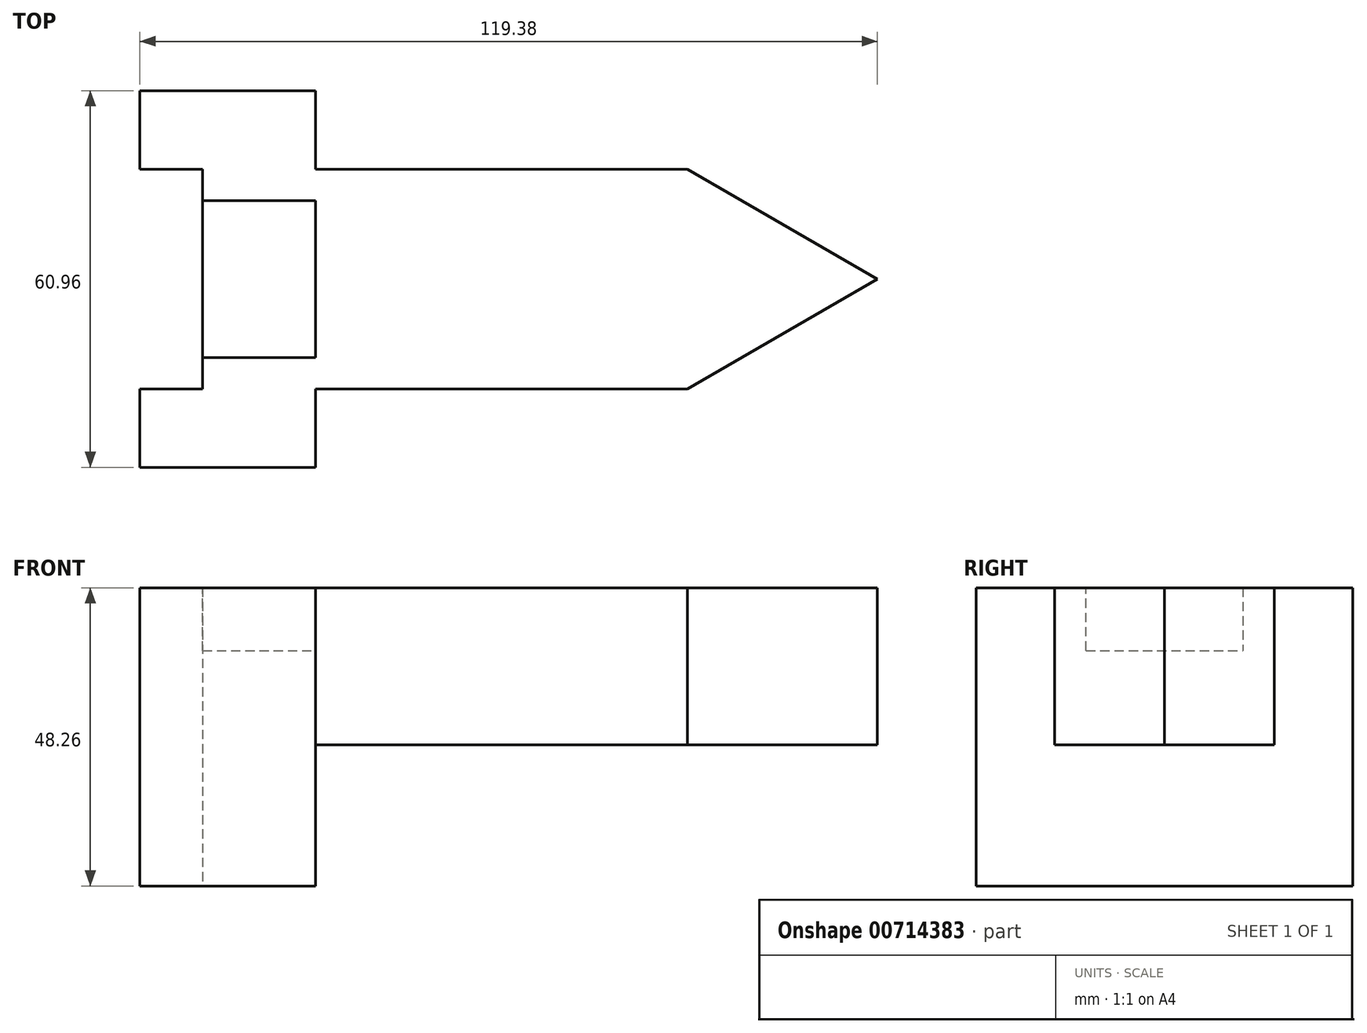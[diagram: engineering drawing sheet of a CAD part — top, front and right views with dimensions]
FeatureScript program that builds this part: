
annotation { "Feature Type Name" : "Feature", "Feature Type Description" : "" }
export const myFeature = defineFeature(function(context is Context, id is Id, definition is map)
    precondition{}
    {
        {
            var Q0;
            Q0=qCreatedBy(makeId("Top.planeOp"),FACE);
            var sketch = newSketch(context, id + "F0", { "sketchPlane" : qUnion([Q0])});
            skLineSegment(sketch, "E0", {"start": v(0, 0) * mm, "end": v(-28.45, 0) * mm});
            skLineSegment(sketch, "E1", {"start": v(-28.45, 0) * mm, "end": v(-28.45, 12.7) * mm});
            skLineSegment(sketch, "E2", {"start": v(-28.45, 12.7) * mm, "end": v(-18.29, 12.7) * mm});
            skLineSegment(sketch, "E3", {"start": v(-18.29, 12.7) * mm, "end": v(-18.29, 17.78) * mm});
            skLineSegment(sketch, "E4", {"start": v(0, 0) * mm, "end": v(0, 30.48) * mm});
            skLineSegment(sketch, "E5", {"start": v(-18.29, 30.48) * mm, "end": v(-18.29, 17.78) * mm});
            skLineSegment(sketch, "E6.MirrorCS", {"start": v(-18.29, 30.48) * mm, "end": v(-18.29, 43.18) * mm});
            skLineSegment(sketch, "E7.MirrorCS", {"start": v(-18.29, 48.26) * mm, "end": v(-18.29, 43.18) * mm});
            skLineSegment(sketch, "E8.MirrorCS", {"start": v(-28.45, 48.26) * mm, "end": v(-18.29, 48.26) * mm});
            skLineSegment(sketch, "E9.MirrorCS", {"start": v(-28.45, 60.96) * mm, "end": v(-28.45, 48.26) * mm});
            skLineSegment(sketch, "E10.MirrorCS", {"start": v(0, 60.96) * mm, "end": v(-28.45, 60.96) * mm});
            skLineSegment(sketch, "E11.MirrorCS", {"start": v(0, 60.96) * mm, "end": v(0, 30.48) * mm});
            skSolve(sketch);
        }
        {
            var Q0;
            Q0 = qSketchRegion(id + "F0", true);
            extrude(context, id + "F1", {"entities" : qUnion([Q0]), "depth" : 48.26 * mm, "offsetDistance" : 25.4 * mm});
        }
        {
            var Q0;
            Q0=makeQuery(id+"F1.opExtrude","SWEPT_FACE",FACE,{"disambiguationData":[OSD([sQuery(id+"F0.wireOp",EDGE,"E4"),sQuery(id+"F0.wireOp",EDGE,"E11.MirrorCS")])]});
            var sketch = newSketch(context, id + "F2", { "sketchPlane" : qUnion([Q0])});
            skLineSegment(sketch, "E12", {"start": v(30.48, 38.1) * mm, "end": v(43.18, 38.1) * mm});
            skLineSegment(sketch, "E13", {"start": v(30.48, 38.1) * mm, "end": v(17.78, 38.1) * mm});
            skLineSegment(sketch, "E14", {"start": v(17.78, 48.26) * mm, "end": v(17.78, 38.1) * mm});
            skLineSegment(sketch, "E15", {"start": v(43.18, 38.1) * mm, "end": v(43.18, 48.26) * mm});
            skLineSegment(sketch, "E16", {"start": v(17.78, 48.26) * mm, "end": v(43.18, 48.26) * mm});
            skSolve(sketch);
        }
        {
            var Q0;
            Q0 = qSketchRegion(id + "F2", true);
            extrude(context, id + "F3", {"entities" : qUnion([Q0]), "operationType" : NewBodyOperationType.REMOVE, "endBound" : BoundingType.UP_TO_NEXT, "oppositeDirection" : true, "depth" : 25.4 * mm, "offsetDistance" : 25.4 * mm});
        }
        {
            var Q0;
            {var subQ0=sQuery(id+"F0.wireOp",EDGE,"E9.MirrorCS");var subQ1=sQuery(id+"F0.wireOp",EDGE,"E8.MirrorCS");var subQ2=sQuery(id+"F0.wireOp",EDGE,"E11.MirrorCS");var subQ3=sQuery(id+"F0.wireOp",EDGE,"E4");var subQ4=sQuery(id+"F0.wireOp",EDGE,"E7.MirrorCS");var subQ5=sQuery(id+"F0.wireOp",EDGE,"E6.MirrorCS");var subQ6=sQuery(id+"F0.wireOp",EDGE,"E5");var subQ7=sQuery(id+"F0.wireOp",EDGE,"E3");var subQ8=sQuery(id+"F0.wireOp",EDGE,"E10.MirrorCS");Q0=makeQuery(id+"F3.boolean.opBoolean","SPLIT",FACE,{"disambiguationData":[TD([makeQuery(id+"F1.opExtrude","SWEPT_FACE",FACE,{"disambiguationData":[OSD([subQ1])]})])],"derivedFrom":makeQuery(id+"F1.opExtrude","CAP_FACE",FACE,{"disambiguationData":[OSD([sQuery(id+"F0.wireOp",EDGE,"E0"),sQuery(id+"F0.wireOp",EDGE,"E1"),sQuery(id+"F0.wireOp",EDGE,"E2"),subQ7,subQ3,subQ6,subQ5,subQ4,subQ1,subQ0,subQ8,subQ2])],"isStart":false})});}
            var sketch = newSketch(context, id + "F4", { "sketchPlane" : qUnion([Q0])});
            skLineSegment(sketch, "E17", {"start": v(0, 30.48) * mm, "end": v(0, 48.26) * mm});
            skLineSegment(sketch, "E18", {"start": v(0, 48.26) * mm, "end": v(60.2, 48.26) * mm});
            skLineSegment(sketch, "E19", {"start": v(60.2, 48.26) * mm, "end": v(90.93, 30.48) * mm});
            skLineSegment(sketch, "E20", {"start": v(0, 30.48) * mm, "end": v(0, 12.7) * mm});
            skLineSegment(sketch, "E21", {"start": v(0, 12.7) * mm, "end": v(60.2, 12.7) * mm});
            skLineSegment(sketch, "E22", {"start": v(60.2, 12.7) * mm, "end": v(90.93, 30.48) * mm});
            skSolve(sketch);
        }
        {
            var Q0;
            {var subQ0=sQuery(id+"F4.wireOp",EDGE,"E18");Q0=makeQuery(id+"F4.imprint","IMPRINT",FACE,{"disambiguationData":[TD([[makeQuery(id+"F4.imprint","IMPRINT",EDGE,{"derivedFrom":subQ0}),-1.0]])]});}
            extrude(context, id + "F5", {"entities" : qUnion([Q0]), "operationType" : NewBodyOperationType.ADD, "oppositeDirection" : true, "depth" : 25.4 * mm, "offsetDistance" : 25.4 * mm});
        }
    });
